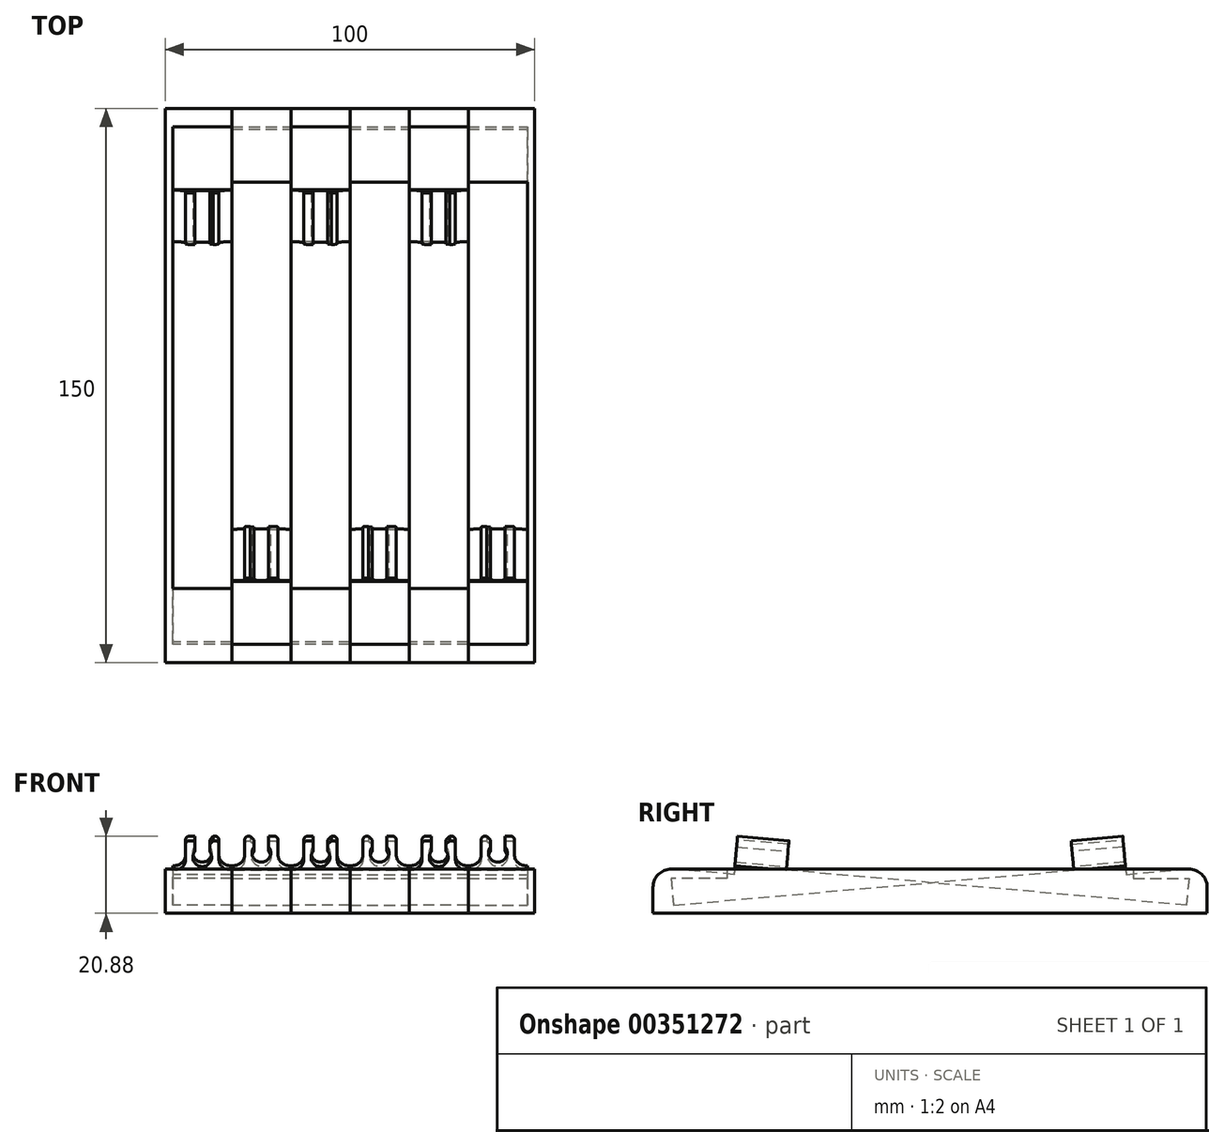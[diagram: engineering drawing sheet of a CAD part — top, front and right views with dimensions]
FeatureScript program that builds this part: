
annotation { "Feature Type Name" : "Feature", "Feature Type Description" : "" }
export const myFeature = defineFeature(function(context is Context, id is Id, definition is map)
    precondition{}
    {
        {
            var Q0;
            Q0=qCreatedBy(makeId("Right.planeOp"),FACE);
            var sketch = newSketch(context, id + "F0", { "sketchPlane" : qUnion([Q0])});
            skLineSegment(sketch, "E0", {"start": v(0, 0) * mm, "end": v(0, 7) * mm});
            skLineSegment(sketch, "E1", {"start": v(5, 12) * mm, "end": v(20, 12) * mm});
            skLineSegment(sketch, "E2", {"start": v(20, 12) * mm, "end": v(20, 9.5) * mm});
            skLineSegment(sketch, "E3", {"start": v(20, 9.5) * mm, "end": v(5.06, 8.2) * mm, "construction": true});
            skLineSegment(sketch, "E4", {"start": v(4.94, 9.5) * mm, "end": v(5.58, 2.22) * mm});
            skLineSegment(sketch, "E5", {"start": v(5.58, 2.22) * mm, "end": v(113.9, 11.7) * mm});
            skLineSegment(sketch, "E6", {"start": v(150, 7) * mm, "end": v(150, 0) * mm});
            skLineSegment(sketch, "E7", {"start": v(150, 0) * mm, "end": v(0, 0) * mm});
            skLineSegment(sketch, "E8", {"start": v(113.9, 11.7) * mm, "end": v(113.2, 19.66) * mm});
            skLineSegment(sketch, "E9", {"start": v(113.2, 19.66) * mm, "end": v(127.14, 20.88) * mm});
            skLineSegment(sketch, "E10", {"start": v(127.14, 20.88) * mm, "end": v(128.05, 10.52) * mm});
            skPoint(sketch, "E11.visualSharp", {"position": v(0, 12) * mm});
            skArc(sketch, "E11.filletArc", {"start": v(5, 12) * mm, "mid": v(1.46, 10.54) * mm, "end": v(0, 7) * mm});
            skPoint(sketch, "E12.visualSharp", {"position": v(150, 12) * mm});
            skLineSegment(sketch, "E13", {"start": v(20, 9.5) * mm, "end": v(4.94, 9.5) * mm});
            skLineSegment(sketch, "E14", {"start": v(128.05, 10.52) * mm, "end": v(145, 12) * mm});
            skLineSegment(sketch, "E15", {"start": v(145, 12) * mm, "end": v(145, 12) * mm});
            skArc(sketch, "E16.filletArc", {"start": v(150, 7) * mm, "mid": v(148.54, 10.54) * mm, "end": v(145, 12) * mm});
            skSolve(sketch);
        }
        {
            var Q0;
            Q0 = qSketchRegion(id + "F0", true);
            extrude(context, id + "F1", {"entities" : qUnion([Q0]), "depth" : 16 * mm});
        }
        {
            var Q0;
            Q0=makeQuery(id+"F1.opExtrude","SWEPT_FACE",FACE,{"disambiguationData":[OSD([sQuery(id+"F0.wireOp",EDGE,"E8")])]});
            var sketch = newSketch(context, id + "F2", { "sketchPlane" : qUnion([Q0])});
            skLineSegment(sketch, "E17", {"start": v(8, 1.72) * mm, "end": v(8, 9.72) * mm, "construction": true});
            skArc(sketch, "E18", {"start": v(6, 6.8) * mm, "mid": v(8, 2.67) * mm, "end": v(10, 6.8) * mm});
            skLineSegment(sketch, "E19", {"start": v(12.5, 8.72) * mm, "end": v(12.5, 4.72) * mm});
            skLineSegment(sketch, "E20", {"start": v(15.5, 1.72) * mm, "end": v(18.5, 1.72) * mm});
            skLineSegment(sketch, "E21", {"start": v(18.5, 1.72) * mm, "end": v(18.5, 10.72) * mm});
            skLineSegment(sketch, "E22", {"start": v(3.5, 8.72) * mm, "end": v(3.5, 4.72) * mm});
            skLineSegment(sketch, "E23", {"start": v(0.5, 1.72) * mm, "end": v(-2.5, 1.72) * mm});
            skLineSegment(sketch, "E24", {"start": v(-2.5, 1.72) * mm, "end": v(-2.5, 10.72) * mm});
            skLineSegment(sketch, "E25", {"start": v(-2.5, 10.72) * mm, "end": v(18.5, 10.72) * mm});
            skLineSegment(sketch, "E26", {"start": v(8, 5.22) * mm, "end": v(6, 5.22) * mm, "construction": true});
            skLineSegment(sketch, "E27", {"start": v(6, 6.8) * mm, "end": v(6, 9.72) * mm});
            skLineSegment(sketch, "E28", {"start": v(8, 5.22) * mm, "end": v(10, 5.22) * mm, "construction": true});
            skLineSegment(sketch, "E29", {"start": v(10, 6.8) * mm, "end": v(10, 9.72) * mm});
            skPoint(sketch, "E30.orphan", {"position": v(3.5, 5.22) * mm});
            skPoint(sketch, "E31.orphan", {"position": v(12.5, 5.22) * mm});
            skLineSegment(sketch, "E32", {"start": v(6, 9.72) * mm, "end": v(4.5, 9.72) * mm});
            skLineSegment(sketch, "E33", {"start": v(10, 9.72) * mm, "end": v(11.5, 9.72) * mm});
            skPoint(sketch, "E34.visualSharp", {"position": v(3.5, 1.72) * mm});
            skArc(sketch, "E34.filletArc", {"start": v(0.5, 1.72) * mm, "mid": v(2.62, 2.6) * mm, "end": v(3.5, 4.72) * mm});
            skPoint(sketch, "E35.visualSharp", {"position": v(12.5, 1.72) * mm});
            skArc(sketch, "E35.filletArc", {"start": v(12.5, 4.72) * mm, "mid": v(13.38, 2.6) * mm, "end": v(15.5, 1.72) * mm});
            skPoint(sketch, "E36.visualSharp", {"position": v(3.5, 9.72) * mm});
            skArc(sketch, "E36.filletArc", {"start": v(4.5, 9.72) * mm, "mid": v(3.8, 9.43) * mm, "end": v(3.5, 8.72) * mm});
            skPoint(sketch, "E37.visualSharp", {"position": v(12.5, 9.72) * mm});
            skArc(sketch, "E37.filletArc", {"start": v(12.5, 8.72) * mm, "mid": v(12.2, 9.43) * mm, "end": v(11.5, 9.72) * mm});
            skSolve(sketch);
        }
        {
            var Q0;
            Q0 = qSketchRegion(id + "F2", true);
            extrude(context, id + "F3", {"entities" : qUnion([Q0]), "operationType" : NewBodyOperationType.REMOVE, "oppositeDirection" : true, "depth" : 25 * mm});
        }
        {
            var Q0;
            Q0=makeQuery(id+"F3.boolean.opBoolean","COPY",EDGE,{"derivedFrom":makeQuery(id+"F3.opExtrude","SWEPT_EDGE",EDGE,{"disambiguationData":[OSD([sQuery(id+"F0.wireOp",EDGE,"E8"),sQuery(id+"F0.wireOp",EDGE,"E9"),sQuery(id+"F2.wireOp",EDGE,"E27"),sQuery(id+"F2.wireOp",EDGE,"E32")])]})});
            var Q1;
            Q1=makeQuery(id+"F3.boolean.opBoolean","COPY",EDGE,{"derivedFrom":makeQuery(id+"F3.opExtrude","SWEPT_EDGE",EDGE,{"disambiguationData":[OSD([sQuery(id+"F0.wireOp",EDGE,"E8"),sQuery(id+"F0.wireOp",EDGE,"E9"),sQuery(id+"F2.wireOp",EDGE,"E29"),sQuery(id+"F2.wireOp",EDGE,"E33")])]})});
            chamfer(context, id + "F4", {"entities" : qUnion([Q0, Q1]), "width" : 1 * mm, "tangentPropagation" : true});
        }
        {
            var Q0;
            Q0=makeQuery(id+"F1.opExtrude","SWEPT_BODY",BODY,{"disambiguationData":[OSD([sQuery(id+"F0.wireOp",EDGE,"E0"),sQuery(id+"F0.wireOp",EDGE,"E1"),sQuery(id+"F0.wireOp",EDGE,"E2"),sQuery(id+"F0.wireOp",EDGE,"E4"),sQuery(id+"F0.wireOp",EDGE,"E5"),sQuery(id+"F0.wireOp",EDGE,"E6"),sQuery(id+"F0.wireOp",EDGE,"E7"),sQuery(id+"F0.wireOp",EDGE,"E8"),sQuery(id+"F0.wireOp",EDGE,"E9"),sQuery(id+"F0.wireOp",EDGE,"E10"),sQuery(id+"F0.wireOp",EDGE,"Y9S6pfHg-R41R-CDvD-xWL7-1D2eYxtCf16d"),sQuery(id+"F0.wireOp",EDGE,"E11.filletArc"),sQuery(id+"F0.wireOp",EDGE,"E12.filletArc"),sQuery(id+"F0.wireOp",EDGE,"E13")])]});
            transform(context, id + "F5", {"entities" : qUnion([Q0]), "transformType" : TransformType.TRANSLATION_3D, "dx" : 32 * mm, "dy" : 0 * mm, "dz" : 0 * mm, "makeCopy" : true});
        }
        {
            var Q0;
            Q0=makeQuery(id+"F5.opPattern","COPY",BODY,{"derivedFrom":makeQuery(id+"F1.opExtrude","SWEPT_BODY",BODY,{"disambiguationData":[OSD([sQuery(id+"F0.wireOp",EDGE,"E0"),sQuery(id+"F0.wireOp",EDGE,"E1"),sQuery(id+"F0.wireOp",EDGE,"E2"),sQuery(id+"F0.wireOp",EDGE,"E4"),sQuery(id+"F0.wireOp",EDGE,"E5"),sQuery(id+"F0.wireOp",EDGE,"E6"),sQuery(id+"F0.wireOp",EDGE,"E7"),sQuery(id+"F0.wireOp",EDGE,"E8"),sQuery(id+"F0.wireOp",EDGE,"E9"),sQuery(id+"F0.wireOp",EDGE,"E10"),sQuery(id+"F0.wireOp",EDGE,"Y9S6pfHg-R41R-CDvD-xWL7-1D2eYxtCf16d"),sQuery(id+"F0.wireOp",EDGE,"E11.filletArc"),sQuery(id+"F0.wireOp",EDGE,"E12.filletArc"),sQuery(id+"F0.wireOp",EDGE,"E13")])]}),"instanceName":"1"});
            transform(context, id + "F6", {"entities" : qUnion([Q0]), "transformType" : TransformType.TRANSLATION_3D, "dx" : 32 * mm, "dy" : 0 * mm, "dz" : 0 * mm, "makeCopy" : true});
        }
        {
            var Q0;
            Q0=makeQuery(id+"F1.opExtrude","SWEPT_BODY",BODY,{"disambiguationData":[OSD([sQuery(id+"F0.wireOp",EDGE,"E0"),sQuery(id+"F0.wireOp",EDGE,"E1"),sQuery(id+"F0.wireOp",EDGE,"E2"),sQuery(id+"F0.wireOp",EDGE,"E4"),sQuery(id+"F0.wireOp",EDGE,"E5"),sQuery(id+"F0.wireOp",EDGE,"E6"),sQuery(id+"F0.wireOp",EDGE,"E7"),sQuery(id+"F0.wireOp",EDGE,"E8"),sQuery(id+"F0.wireOp",EDGE,"E9"),sQuery(id+"F0.wireOp",EDGE,"E10"),sQuery(id+"F0.wireOp",EDGE,"Y9S6pfHg-R41R-CDvD-xWL7-1D2eYxtCf16d"),sQuery(id+"F0.wireOp",EDGE,"E11.filletArc"),sQuery(id+"F0.wireOp",EDGE,"E12.filletArc"),sQuery(id+"F0.wireOp",EDGE,"E13")])]});
            transform(context, id + "F7", {"entities" : qUnion([Q0]), "transformType" : TransformType.TRANSLATION_3D, "dx" : 0 * mm, "dy" : 160 * mm, "dz" : 0 * mm, "makeCopy" : true});
        }
        {
            var Q0;
            Q0=makeQuery(id+"F5.opPattern","COPY",BODY,{"derivedFrom":makeQuery(id+"F1.opExtrude","SWEPT_BODY",BODY,{"disambiguationData":[OSD([sQuery(id+"F0.wireOp",EDGE,"E0"),sQuery(id+"F0.wireOp",EDGE,"E1"),sQuery(id+"F0.wireOp",EDGE,"E2"),sQuery(id+"F0.wireOp",EDGE,"E4"),sQuery(id+"F0.wireOp",EDGE,"E5"),sQuery(id+"F0.wireOp",EDGE,"E6"),sQuery(id+"F0.wireOp",EDGE,"E7"),sQuery(id+"F0.wireOp",EDGE,"E8"),sQuery(id+"F0.wireOp",EDGE,"E9"),sQuery(id+"F0.wireOp",EDGE,"E10"),sQuery(id+"F0.wireOp",EDGE,"Y9S6pfHg-R41R-CDvD-xWL7-1D2eYxtCf16d"),sQuery(id+"F0.wireOp",EDGE,"E11.filletArc"),sQuery(id+"F0.wireOp",EDGE,"E12.filletArc"),sQuery(id+"F0.wireOp",EDGE,"E13")])]}),"instanceName":"1"});
            transform(context, id + "F8", {"entities" : qUnion([Q0]), "transformType" : TransformType.TRANSLATION_3D, "dx" : 0 * mm, "dy" : 160 * mm, "dz" : 0 * mm, "makeCopy" : true});
        }
        {
            var Q0;
            Q0=makeQuery(id+"F6.opPattern","COPY",BODY,{"derivedFrom":makeQuery(id+"F5.opPattern","COPY",BODY,{"derivedFrom":makeQuery(id+"F1.opExtrude","SWEPT_BODY",BODY,{"disambiguationData":[OSD([sQuery(id+"F0.wireOp",EDGE,"E0"),sQuery(id+"F0.wireOp",EDGE,"E1"),sQuery(id+"F0.wireOp",EDGE,"E2"),sQuery(id+"F0.wireOp",EDGE,"E4"),sQuery(id+"F0.wireOp",EDGE,"E5"),sQuery(id+"F0.wireOp",EDGE,"E6"),sQuery(id+"F0.wireOp",EDGE,"E7"),sQuery(id+"F0.wireOp",EDGE,"E8"),sQuery(id+"F0.wireOp",EDGE,"E9"),sQuery(id+"F0.wireOp",EDGE,"E10"),sQuery(id+"F0.wireOp",EDGE,"Y9S6pfHg-R41R-CDvD-xWL7-1D2eYxtCf16d"),sQuery(id+"F0.wireOp",EDGE,"E11.filletArc"),sQuery(id+"F0.wireOp",EDGE,"E12.filletArc"),sQuery(id+"F0.wireOp",EDGE,"E13")])]}),"instanceName":"1"}),"instanceName":"1"});
            transform(context, id + "F9", {"entities" : qUnion([Q0]), "transformType" : TransformType.TRANSLATION_3D, "dx" : 0 * mm, "dy" : 160 * mm, "dz" : 0 * mm, "makeCopy" : true});
        }
        {
            var Q0;
            Q0=qCreatedBy(makeId("Right.planeOp"),FACE);
            var sketch = newSketch(context, id + "F10", { "sketchPlane" : qUnion([Q0])});
            skLineSegment(sketch, "E38", {"start": v(0, 0) * mm, "end": v(0, 50) * mm, "construction": true});
            skSolve(sketch);
        }
        {
            var Q0;
            Q0=makeQuery(id+"F8.opPattern","COPY",BODY,{"derivedFrom":makeQuery(id+"F5.opPattern","COPY",BODY,{"derivedFrom":makeQuery(id+"F1.opExtrude","SWEPT_BODY",BODY,{"disambiguationData":[OSD([sQuery(id+"F0.wireOp",EDGE,"E0"),sQuery(id+"F0.wireOp",EDGE,"E1"),sQuery(id+"F0.wireOp",EDGE,"E2"),sQuery(id+"F0.wireOp",EDGE,"E4"),sQuery(id+"F0.wireOp",EDGE,"E5"),sQuery(id+"F0.wireOp",EDGE,"E6"),sQuery(id+"F0.wireOp",EDGE,"E7"),sQuery(id+"F0.wireOp",EDGE,"E8"),sQuery(id+"F0.wireOp",EDGE,"E9"),sQuery(id+"F0.wireOp",EDGE,"E10"),sQuery(id+"F0.wireOp",EDGE,"Y9S6pfHg-R41R-CDvD-xWL7-1D2eYxtCf16d"),sQuery(id+"F0.wireOp",EDGE,"E11.filletArc"),sQuery(id+"F0.wireOp",EDGE,"E12.filletArc"),sQuery(id+"F0.wireOp",EDGE,"E13")])]}),"instanceName":"1"}),"instanceName":"1"});
            var Q1;
            Q1=makeQuery(id+"F9.opPattern","COPY",BODY,{"derivedFrom":makeQuery(id+"F6.opPattern","COPY",BODY,{"derivedFrom":makeQuery(id+"F5.opPattern","COPY",BODY,{"derivedFrom":makeQuery(id+"F1.opExtrude","SWEPT_BODY",BODY,{"disambiguationData":[OSD([sQuery(id+"F0.wireOp",EDGE,"E0"),sQuery(id+"F0.wireOp",EDGE,"E1"),sQuery(id+"F0.wireOp",EDGE,"E2"),sQuery(id+"F0.wireOp",EDGE,"E4"),sQuery(id+"F0.wireOp",EDGE,"E5"),sQuery(id+"F0.wireOp",EDGE,"E6"),sQuery(id+"F0.wireOp",EDGE,"E7"),sQuery(id+"F0.wireOp",EDGE,"E8"),sQuery(id+"F0.wireOp",EDGE,"E9"),sQuery(id+"F0.wireOp",EDGE,"E10"),sQuery(id+"F0.wireOp",EDGE,"Y9S6pfHg-R41R-CDvD-xWL7-1D2eYxtCf16d"),sQuery(id+"F0.wireOp",EDGE,"E11.filletArc"),sQuery(id+"F0.wireOp",EDGE,"E12.filletArc"),sQuery(id+"F0.wireOp",EDGE,"E13")])]}),"instanceName":"1"}),"instanceName":"1"}),"instanceName":"1"});
            var Q2;
            Q2=makeQuery(id+"F7.opPattern","COPY",BODY,{"derivedFrom":makeQuery(id+"F1.opExtrude","SWEPT_BODY",BODY,{"disambiguationData":[OSD([sQuery(id+"F0.wireOp",EDGE,"E0"),sQuery(id+"F0.wireOp",EDGE,"E1"),sQuery(id+"F0.wireOp",EDGE,"E2"),sQuery(id+"F0.wireOp",EDGE,"E4"),sQuery(id+"F0.wireOp",EDGE,"E5"),sQuery(id+"F0.wireOp",EDGE,"E6"),sQuery(id+"F0.wireOp",EDGE,"E7"),sQuery(id+"F0.wireOp",EDGE,"E8"),sQuery(id+"F0.wireOp",EDGE,"E9"),sQuery(id+"F0.wireOp",EDGE,"E10"),sQuery(id+"F0.wireOp",EDGE,"Y9S6pfHg-R41R-CDvD-xWL7-1D2eYxtCf16d"),sQuery(id+"F0.wireOp",EDGE,"E11.filletArc"),sQuery(id+"F0.wireOp",EDGE,"E12.filletArc"),sQuery(id+"F0.wireOp",EDGE,"E13")])]}),"instanceName":"1"});
            var Q3;
            Q3=sQuery(id+"F10.wireOp",EDGE,"E38");
            transform(context, id + "F11", {"entities" : qUnion([Q0, Q1, Q2]), "transformType" : TransformType.ROTATION, "transformAxis" : qUnion([Q3]), "angle" : 180 * degree, "makeCopy" : false});
        }
        {
            var Q0;
            Q0=makeQuery(id+"F7.opPattern","COPY",BODY,{"derivedFrom":makeQuery(id+"F1.opExtrude","SWEPT_BODY",BODY,{"disambiguationData":[OSD([sQuery(id+"F0.wireOp",EDGE,"E0"),sQuery(id+"F0.wireOp",EDGE,"E1"),sQuery(id+"F0.wireOp",EDGE,"E2"),sQuery(id+"F0.wireOp",EDGE,"E4"),sQuery(id+"F0.wireOp",EDGE,"E5"),sQuery(id+"F0.wireOp",EDGE,"E6"),sQuery(id+"F0.wireOp",EDGE,"E7"),sQuery(id+"F0.wireOp",EDGE,"E8"),sQuery(id+"F0.wireOp",EDGE,"E9"),sQuery(id+"F0.wireOp",EDGE,"E10"),sQuery(id+"F0.wireOp",EDGE,"Y9S6pfHg-R41R-CDvD-xWL7-1D2eYxtCf16d"),sQuery(id+"F0.wireOp",EDGE,"E11.filletArc"),sQuery(id+"F0.wireOp",EDGE,"E12.filletArc"),sQuery(id+"F0.wireOp",EDGE,"E13")])]}),"instanceName":"1"});
            var Q1;
            Q1=makeQuery(id+"F8.opPattern","COPY",BODY,{"derivedFrom":makeQuery(id+"F5.opPattern","COPY",BODY,{"derivedFrom":makeQuery(id+"F1.opExtrude","SWEPT_BODY",BODY,{"disambiguationData":[OSD([sQuery(id+"F0.wireOp",EDGE,"E0"),sQuery(id+"F0.wireOp",EDGE,"E1"),sQuery(id+"F0.wireOp",EDGE,"E2"),sQuery(id+"F0.wireOp",EDGE,"E4"),sQuery(id+"F0.wireOp",EDGE,"E5"),sQuery(id+"F0.wireOp",EDGE,"E6"),sQuery(id+"F0.wireOp",EDGE,"E7"),sQuery(id+"F0.wireOp",EDGE,"E8"),sQuery(id+"F0.wireOp",EDGE,"E9"),sQuery(id+"F0.wireOp",EDGE,"E10"),sQuery(id+"F0.wireOp",EDGE,"Y9S6pfHg-R41R-CDvD-xWL7-1D2eYxtCf16d"),sQuery(id+"F0.wireOp",EDGE,"E11.filletArc"),sQuery(id+"F0.wireOp",EDGE,"E12.filletArc"),sQuery(id+"F0.wireOp",EDGE,"E13")])]}),"instanceName":"1"}),"instanceName":"1"});
            var Q2;
            Q2=makeQuery(id+"F9.opPattern","COPY",BODY,{"derivedFrom":makeQuery(id+"F6.opPattern","COPY",BODY,{"derivedFrom":makeQuery(id+"F5.opPattern","COPY",BODY,{"derivedFrom":makeQuery(id+"F1.opExtrude","SWEPT_BODY",BODY,{"disambiguationData":[OSD([sQuery(id+"F0.wireOp",EDGE,"E0"),sQuery(id+"F0.wireOp",EDGE,"E1"),sQuery(id+"F0.wireOp",EDGE,"E2"),sQuery(id+"F0.wireOp",EDGE,"E4"),sQuery(id+"F0.wireOp",EDGE,"E5"),sQuery(id+"F0.wireOp",EDGE,"E6"),sQuery(id+"F0.wireOp",EDGE,"E7"),sQuery(id+"F0.wireOp",EDGE,"E8"),sQuery(id+"F0.wireOp",EDGE,"E9"),sQuery(id+"F0.wireOp",EDGE,"E10"),sQuery(id+"F0.wireOp",EDGE,"Y9S6pfHg-R41R-CDvD-xWL7-1D2eYxtCf16d"),sQuery(id+"F0.wireOp",EDGE,"E11.filletArc"),sQuery(id+"F0.wireOp",EDGE,"E12.filletArc"),sQuery(id+"F0.wireOp",EDGE,"E13")])]}),"instanceName":"1"}),"instanceName":"1"}),"instanceName":"1"});
            transform(context, id + "F12", {"entities" : qUnion([Q0, Q1, Q2]), "transformType" : TransformType.TRANSLATION_3D, "dx" : 96 * mm, "dy" : 310 * mm, "dz" : 0 * mm, "makeCopy" : false});
        }
        {
            var Q0;
            Q0=makeQuery(id+"F7.opPattern","COPY",FACE,{"derivedFrom":makeQuery(id+"F1.opExtrude","CAP_FACE",FACE,{"disambiguationData":[OSD([sQuery(id+"F0.wireOp",EDGE,"E0"),sQuery(id+"F0.wireOp",EDGE,"E1"),sQuery(id+"F0.wireOp",EDGE,"E2"),sQuery(id+"F0.wireOp",EDGE,"E4"),sQuery(id+"F0.wireOp",EDGE,"E5"),sQuery(id+"F0.wireOp",EDGE,"E6"),sQuery(id+"F0.wireOp",EDGE,"E7"),sQuery(id+"F0.wireOp",EDGE,"E8"),sQuery(id+"F0.wireOp",EDGE,"E9"),sQuery(id+"F0.wireOp",EDGE,"E10"),sQuery(id+"F0.wireOp",EDGE,"E11.filletArc"),sQuery(id+"F0.wireOp",EDGE,"E13"),sQuery(id+"F0.wireOp",EDGE,"E14"),sQuery(id+"F0.wireOp",EDGE,"E16.filletArc")])],"isStart":true}),"instanceName":"1"});
            var sketch = newSketch(context, id + "F13", { "sketchPlane" : qUnion([Q0])});
            skPoint(sketch, "E39.oppositeSnap0", {"position": v(150, 3.5) * mm});
            skLineSegment(sketch, "E39.bottom", {"start": v(0, 0) * mm, "end": v(150, 0) * mm});
            skLineSegment(sketch, "E39.top", {"start": v(5, 12) * mm, "end": v(145, 12) * mm});
            skLineSegment(sketch, "E39.left", {"start": v(0, 0) * mm, "end": v(0, 7) * mm});
            skLineSegment(sketch, "E39.right", {"start": v(150, 0) * mm, "end": v(150, 7) * mm});
            skPoint(sketch, "E40.visualSharp", {"position": v(0, 12) * mm});
            skArc(sketch, "E40.filletArc", {"start": v(5, 12) * mm, "mid": v(1.46, 10.54) * mm, "end": v(0, 7) * mm});
            skPoint(sketch, "E41.visualSharp", {"position": v(150, 12) * mm});
            skArc(sketch, "E41.filletArc", {"start": v(150, 7) * mm, "mid": v(148.54, 10.54) * mm, "end": v(145, 12) * mm});
            skSolve(sketch);
        }
        {
            var Q0;
            Q0 = qSketchRegion(id + "F13", true);
            extrude(context, id + "F14", {"entities" : qUnion([Q0]), "operationType" : NewBodyOperationType.ADD, "depth" : 2 * mm});
        }
        {
            var Q0;
            Q0=makeQuery(id+"F1.opExtrude","CAP_FACE",FACE,{"disambiguationData":[OSD([sQuery(id+"F0.wireOp",EDGE,"E0"),sQuery(id+"F0.wireOp",EDGE,"E1"),sQuery(id+"F0.wireOp",EDGE,"E2"),sQuery(id+"F0.wireOp",EDGE,"E4"),sQuery(id+"F0.wireOp",EDGE,"E5"),sQuery(id+"F0.wireOp",EDGE,"E6"),sQuery(id+"F0.wireOp",EDGE,"E7"),sQuery(id+"F0.wireOp",EDGE,"E8"),sQuery(id+"F0.wireOp",EDGE,"E9"),sQuery(id+"F0.wireOp",EDGE,"E10"),sQuery(id+"F0.wireOp",EDGE,"E11.filletArc"),sQuery(id+"F0.wireOp",EDGE,"E13"),sQuery(id+"F0.wireOp",EDGE,"E14"),sQuery(id+"F0.wireOp",EDGE,"E16.filletArc")])],"isStart":true});
            var sketch = newSketch(context, id + "F15", { "sketchPlane" : qUnion([Q0])});
            skLineSegment(sketch, "E42.bottom", {"start": v(0, 0) * mm, "end": v(-150, 0) * mm});
            skLineSegment(sketch, "E42.top", {"start": v(-5, 12) * mm, "end": v(-145, 12) * mm});
            skLineSegment(sketch, "E42.left", {"start": v(0, 0) * mm, "end": v(0, 7) * mm});
            skLineSegment(sketch, "E42.right", {"start": v(-150, 0) * mm, "end": v(-150, 7) * mm});
            skPoint(sketch, "E43.visualSharp", {"position": v(-150, 12) * mm});
            skArc(sketch, "E43.filletArc", {"start": v(-145, 12) * mm, "mid": v(-148.54, 10.54) * mm, "end": v(-150, 7) * mm});
            skPoint(sketch, "E44.visualSharp", {"position": v(0, 12) * mm});
            skArc(sketch, "E44.filletArc", {"start": v(0, 7) * mm, "mid": v(-1.46, 10.54) * mm, "end": v(-5, 12) * mm});
            skSolve(sketch);
        }
        {
            var Q0;
            Q0 = qSketchRegion(id + "F15", true);
            extrude(context, id + "F16", {"entities" : qUnion([Q0]), "operationType" : NewBodyOperationType.ADD, "depth" : 2 * mm});
        }
    });
